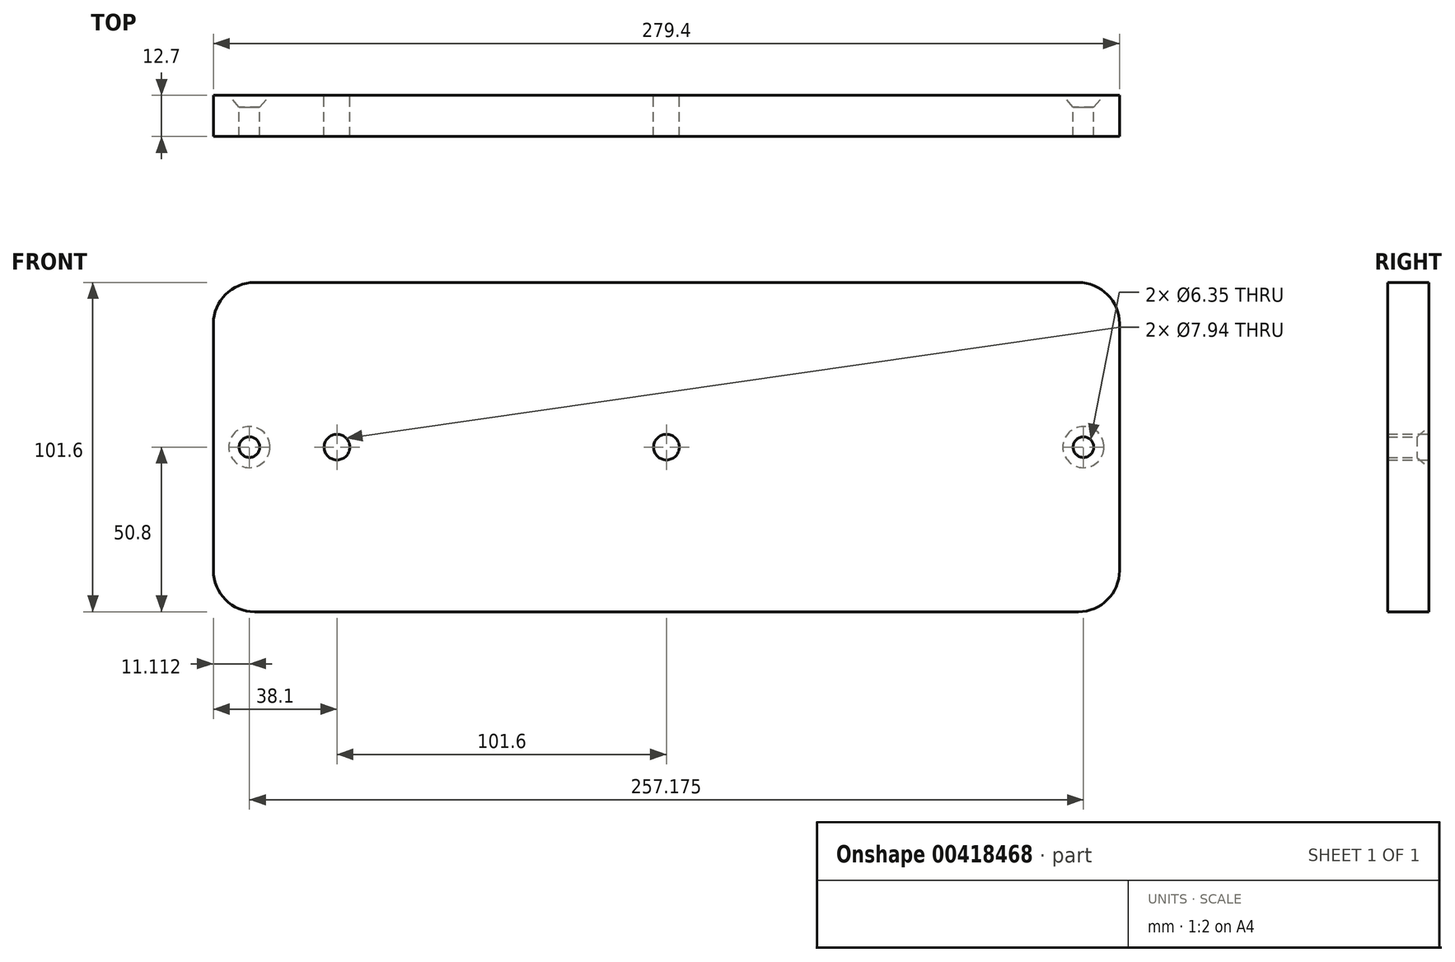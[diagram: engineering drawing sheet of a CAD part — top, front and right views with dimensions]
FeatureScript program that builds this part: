
annotation { "Feature Type Name" : "Feature", "Feature Type Description" : "" }
export const myFeature = defineFeature(function(context is Context, id is Id, definition is map)
    precondition{}
    {
        {
            var Q0;
            Q0=qCreatedBy(makeId("Front.planeOp"),FACE);
            var sketch = newSketch(context, id + "F0", { "sketchPlane" : qUnion([Q0])});
            skLineSegment(sketch, "E0.bottom", {"start": v(-139.7, 0) * mm, "end": v(139.7, 0) * mm});
            skLineSegment(sketch, "E0.top", {"start": v(-139.7, -101.6) * mm, "end": v(139.7, -101.6) * mm});
            skLineSegment(sketch, "E0.left", {"start": v(-139.7, 0) * mm, "end": v(-139.7, -101.6) * mm});
            skLineSegment(sketch, "E0.right", {"start": v(139.7, 0) * mm, "end": v(139.7, -101.6) * mm});
            skLineSegment(sketch, "E1", {"start": v(-139.7, -50.8) * mm, "end": v(139.7, -50.8) * mm, "construction": true});
            skLineSegment(sketch, "E2", {"start": v(-128.59, 0) * mm, "end": v(-128.59, -101.6) * mm, "construction": true});
            skLineSegment(sketch, "E3", {"start": v(128.59, 0) * mm, "end": v(128.59, -101.6) * mm, "construction": true});
            skPoint(sketch, "E4", {"position": v(-128.59, -50.8) * mm});
            skPoint(sketch, "E5", {"position": v(128.59, -50.8) * mm});
            skLineSegment(sketch, "E6", {"start": v(-101.6, 0) * mm, "end": v(-101.6, -101.6) * mm, "construction": true});
            skLineSegment(sketch, "E7", {"start": v(0, 0) * mm, "end": v(0, -101.6) * mm, "construction": true});
            skPoint(sketch, "E8", {"position": v(-101.6, -50.8) * mm});
            skPoint(sketch, "E9", {"position": v(0, -50.8) * mm});
            skSolve(sketch);
        }
        {
            var Q0;
            Q0=makeQuery(id+"F0.imprint","IMPRINT",FACE,{"disambiguationData":[TD([[makeQuery(id+"F0.imprint","IMPRINT",EDGE,{"derivedFrom":sQuery(id+"F0.wireOp",EDGE,"E0.bottom")}),-1.0]])]});
            extrude(context, id + "F1", {"entities" : qUnion([Q0]), "depth" : 12.7 * mm});
        }
        {
            var Q0;
            Q0=sQuery(id+"F0.wireOp",VERTEX,"E4");
            var Q1;
            Q1=sQuery(id+"F0.wireOp",VERTEX,"E5");
            var Q2;
            Q2=makeQuery(id+"F1.opExtrude","SWEPT_BODY",BODY,{"disambiguationData":[OSD([sQuery(id+"F0.wireOp",EDGE,"E0.bottom"),sQuery(id+"F0.wireOp",EDGE,"E0.top"),sQuery(id+"F0.wireOp",EDGE,"E0.left"),sQuery(id+"F0.wireOp",EDGE,"E0.right")])]});
            hole(context, id + "F2", {"style" : HoleStyle.C_SINK, "endStyle" : HoleEndStyle.THROUGH, "oppositeDirection" : true, "holeDiameter" : 6.35 * mm, "cSinkDiameter" : 12.7 * mm, "cSinkAngle" : 82 * degree, "isTappedThrough" : true, "tappedDepth" : 12.7 * mm, "tapClearance" : 3, "locations" : qUnion([Q0, Q1]), "scope" : qUnion([Q2])});
        }
        {
            var Q0;
            Q0=sQuery(id+"F0.wireOp",VERTEX,"E8");
            var Q1;
            Q1=sQuery(id+"F0.wireOp",VERTEX,"E9");
            var Q2;
            Q2=makeQuery(id+"F1.opExtrude","SWEPT_BODY",BODY,{"disambiguationData":[OSD([sQuery(id+"F0.wireOp",EDGE,"E0.bottom"),sQuery(id+"F0.wireOp",EDGE,"E0.top"),sQuery(id+"F0.wireOp",EDGE,"E0.left"),sQuery(id+"F0.wireOp",EDGE,"E0.right")])]});
            hole(context, id + "F3", {"style" : HoleStyle.SIMPLE, "endStyle" : HoleEndStyle.THROUGH, "oppositeDirection" : true, "holeDiameter" : 7.94 * mm, "isTappedThrough" : true, "tappedDepth" : 12.7 * mm, "tapClearance" : 3, "locations" : qUnion([Q0, Q1]), "scope" : qUnion([Q2])});
        }
        {
            var Q0;
            Q0=makeQuery(id+"F1.opExtrude","SWEPT_EDGE",EDGE,{"disambiguationData":[OSD([sQuery(id+"F0.wireOp",EDGE,"E0.bottom"),sQuery(id+"F0.wireOp",EDGE,"E0.right")])]});
            var Q1;
            Q1=makeQuery(id+"F1.opExtrude","SWEPT_EDGE",EDGE,{"disambiguationData":[OSD([sQuery(id+"F0.wireOp",EDGE,"E0.top"),sQuery(id+"F0.wireOp",EDGE,"E0.right")])]});
            var Q2;
            Q2=makeQuery(id+"F1.opExtrude","SWEPT_EDGE",EDGE,{"disambiguationData":[OSD([sQuery(id+"F0.wireOp",EDGE,"E0.top"),sQuery(id+"F0.wireOp",EDGE,"E0.left")])]});
            var Q3;
            Q3=makeQuery(id+"F1.opExtrude","SWEPT_EDGE",EDGE,{"disambiguationData":[OSD([sQuery(id+"F0.wireOp",EDGE,"E0.bottom"),sQuery(id+"F0.wireOp",EDGE,"E0.left")])]});
            fillet(context, id + "F4", {"entities" : qUnion([Q0, Q1, Q2, Q3]), "radius" : 12.7 * mm, "tangentPropagation" : true, "allowEdgeOverflow" : false});
        }
    });
